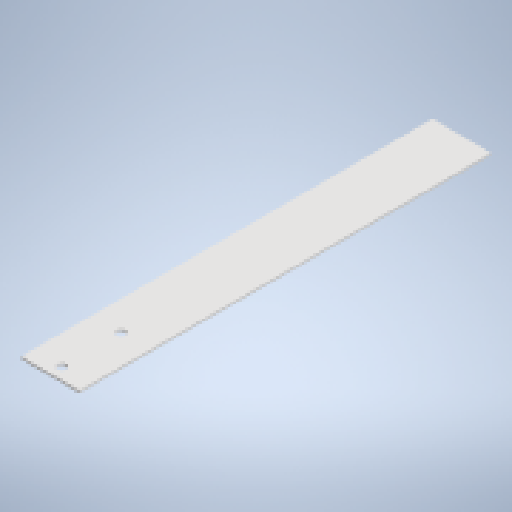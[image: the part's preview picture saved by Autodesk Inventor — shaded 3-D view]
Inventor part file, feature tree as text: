
AUTODESK INVENTOR PART (.ipt)
format: ipt  version: 2023 (Build 270158000, 158)  size: 139,264 bytes
history: native  units: mm
features: extrude x1, sketch x1
ambient origin geometry x8: Origin, YZ Plane, XZ Plane, XY Plane, X Axis, Y Axis, Z Axis, Center Point
bodies: Solid1 (feature_tree)
feature tree (2):
  extrude  "Extrusion1"  Depth=350.0mm
  sketch  "Sketch1"  dims[d0=50.0mm d1=350.0mm d2=10.0mm d3=8.0mm d4=50.0mm d5=8.0mm d6=2.0mm d7=0.0mm]
